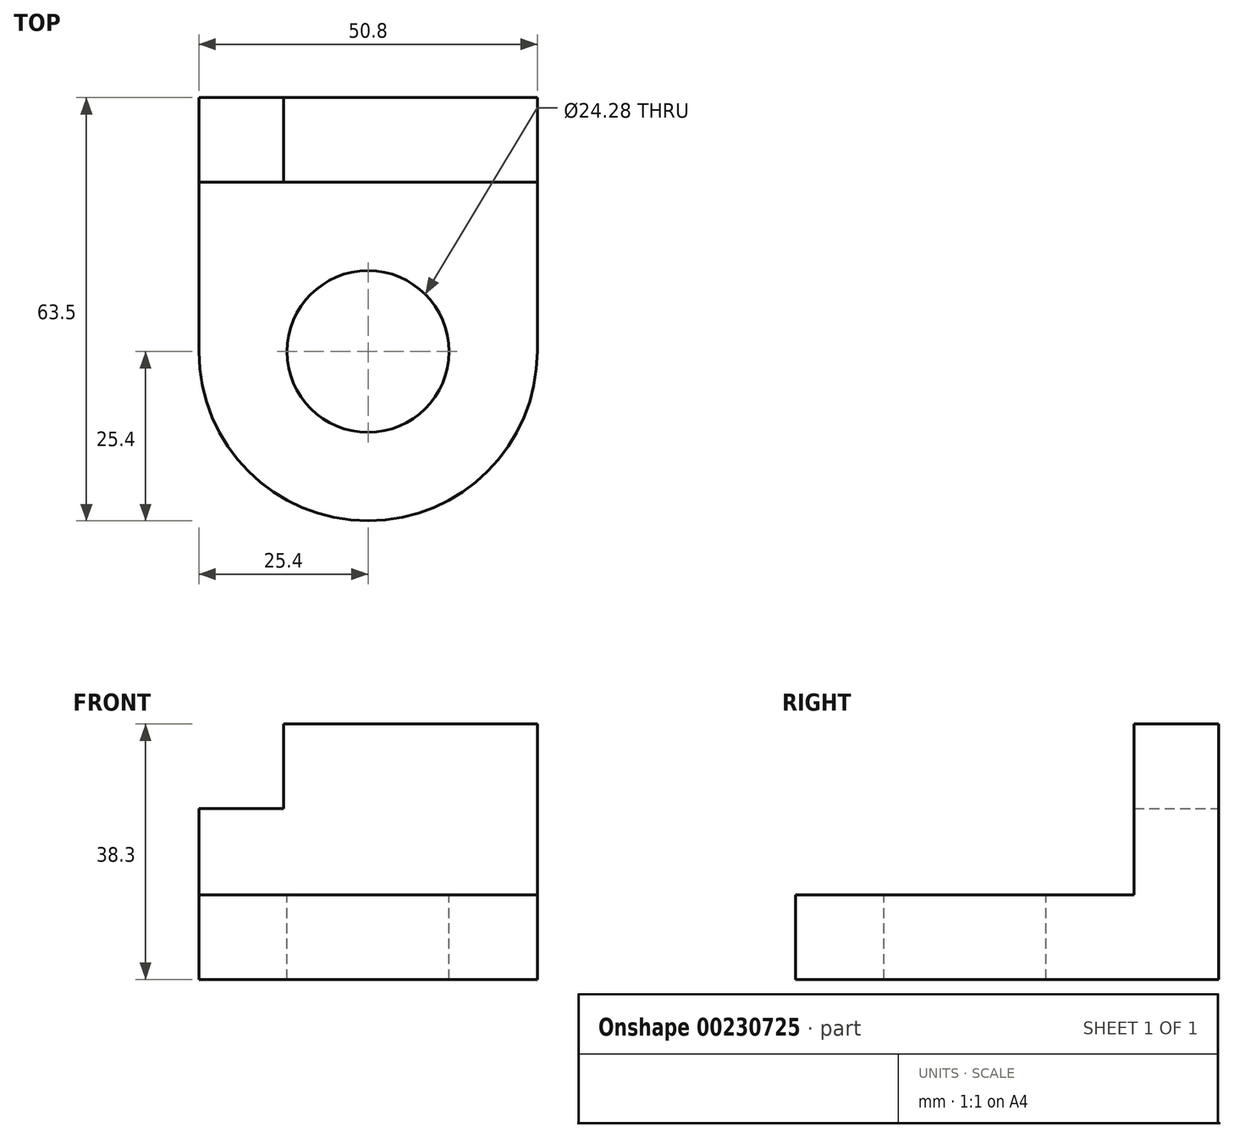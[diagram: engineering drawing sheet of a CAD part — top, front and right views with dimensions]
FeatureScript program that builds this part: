
annotation { "Feature Type Name" : "Feature", "Feature Type Description" : "" }
export const myFeature = defineFeature(function(context is Context, id is Id, definition is map)
    precondition{}
    {
        {
            var Q0;
            Q0=qCreatedBy(makeId("Front.planeOp"),FACE);
            var sketch = newSketch(context, id + "F0", { "sketchPlane" : qUnion([Q0])});
            skLineSegment(sketch, "E0.bottom", {"start": v(25.4, 19.05) * mm, "end": v(-25.4, 19.05) * mm});
            skLineSegment(sketch, "E0.top", {"start": v(25.4, -19.05) * mm, "end": v(-25.4, -19.05) * mm});
            skLineSegment(sketch, "E0.left", {"start": v(25.4, 19.05) * mm, "end": v(25.4, -19.05) * mm});
            skLineSegment(sketch, "E0.right", {"start": v(-25.4, 19.05) * mm, "end": v(-25.4, -19.05) * mm});
            skPoint(sketch, "E0.middle", {"position": v(0, 0) * mm});
            skSolve(sketch);
        }
        {
            var Q0;
            Q0=makeQuery(id+"F0.imprint","IMPRINT",FACE,{"disambiguationData":[TD([[makeQuery(id+"F0.imprint","IMPRINT",EDGE,{"derivedFrom":sQuery(id+"F0.wireOp",EDGE,"E0.bottom")}),1.0]])]});
            extrude(context, id + "F1", {"entities" : qUnion([Q0]), "depth" : 12.7 * mm});
        }
        {
            var Q0;
            Q0=qCreatedBy(makeId("Front.planeOp"),FACE);
            var sketch = newSketch(context, id + "F2", { "sketchPlane" : qUnion([Q0])});
            skLineSegment(sketch, "E1.bottom", {"start": v(-25.4, 19.05) * mm, "end": v(-12.7, 19.05) * mm});
            skLineSegment(sketch, "E1.top", {"start": v(-25.4, 6.35) * mm, "end": v(-12.7, 6.35) * mm});
            skLineSegment(sketch, "E1.left", {"start": v(-25.4, 19.05) * mm, "end": v(-25.4, 6.35) * mm});
            skLineSegment(sketch, "E1.right", {"start": v(-12.7, 19.05) * mm, "end": v(-12.7, 6.35) * mm});
            skSolve(sketch);
        }
        {
            var Q0;
            Q0 = qSketchRegion(id + "F2", true);
            extrude(context, id + "F3", {"entities" : qUnion([Q0]), "operationType" : NewBodyOperationType.REMOVE, "depth" : 12.7 * mm});
        }
        {
            var Q0;
            Q0=qCreatedBy(makeId("Front.planeOp"),FACE);
            var sketch = newSketch(context, id + "F4", { "sketchPlane" : qUnion([Q0])});
            skLineSegment(sketch, "E2.bottom", {"start": v(-25.4, -19.25) * mm, "end": v(25.4, -19.25) * mm});
            skLineSegment(sketch, "E2.top", {"start": v(-25.4, -6.55) * mm, "end": v(25.4, -6.55) * mm});
            skLineSegment(sketch, "E2.left", {"start": v(-25.4, -19.25) * mm, "end": v(-25.4, -6.55) * mm});
            skLineSegment(sketch, "E2.right", {"start": v(25.4, -19.25) * mm, "end": v(25.4, -6.55) * mm});
            skSolve(sketch);
        }
        {
            var Q0;
            Q0 = qSketchRegion(id + "F4", true);
            extrude(context, id + "F5", {"entities" : qUnion([Q0]), "operationType" : NewBodyOperationType.ADD, "depth" : 63.5 * mm});
        }
        {
            var Q0;
            Q0=makeQuery(id+"F5.opExtrude","SWEPT_FACE",FACE,{"disambiguationData":[OSD([sQuery(id+"F4.wireOp",EDGE,"E2.top")])]});
            var sketch = newSketch(context, id + "F6", { "sketchPlane" : qUnion([Q0])});
            skCircle(sketch, "E3", {"center": v(0, -38.1) * mm, "radius": 12.14 * mm});
            skCircle(sketch, "E4", {"center": v(0, -38.1) * mm, "radius": 25.4 * mm});
            skSolve(sketch);
        }
        {
            var Q0;
            {var subQ0=sQuery(id+"F6.wireOp",EDGE,"E4");var subQ1=sQuery(id+"F4.wireOp",EDGE,"E2.top");var subQ4=makeQuery(id+"F5.opExtrude","CAP_EDGE",EDGE,{"disambiguationData":[OSD([subQ1])],"isStart":false});var subQ5=makeQuery(id+"F6.imprint","INTERSECT",VERTEX,{"derivedFrom":[subQ4,subQ0]});Q0=makeQuery(id+"F6.imprint","IMPRINT",FACE,{"disambiguationData":[TD([[makeQuery(id+"F6.imprint","IMPRINT",EDGE,{"disambiguationData":[TD([[subQ5,-1.0]])],"derivedFrom":subQ0}),-1.0]])]});}
            var Q1;
            {var subQ0=sQuery(id+"F6.wireOp",EDGE,"E4");var subQ1=sQuery(id+"F4.wireOp",EDGE,"E2.top");var subQ4=makeQuery(id+"F5.opExtrude","CAP_EDGE",EDGE,{"disambiguationData":[OSD([subQ1])],"isStart":false});var subQ5=makeQuery(id+"F6.imprint","INTERSECT",VERTEX,{"derivedFrom":[subQ4,subQ0]});Q1=makeQuery(id+"F6.imprint","IMPRINT",FACE,{"disambiguationData":[TD([[makeQuery(id+"F6.imprint","IMPRINT",EDGE,{"disambiguationData":[TD([[subQ5,1.0]])],"derivedFrom":subQ0}),-1.0]])]});}
            var Q2;
            Q2=makeQuery(id+"F6.imprint","IMPRINT",FACE,{"disambiguationData":[TD([[makeQuery(id+"F6.imprint","IMPRINT",EDGE,{"derivedFrom":sQuery(id+"F6.wireOp",EDGE,"E3")}),1.0]])]});
            extrude(context, id + "F7", {"entities" : qUnion([Q0, Q1, Q2]), "operationType" : NewBodyOperationType.REMOVE, "endBound" : BoundingType.THROUGH_ALL, "oppositeDirection" : true, "depth" : 25.4 * mm});
        }
    });
